# Revit family: Smoothy 1.6A
name_source: partatom
category: Lighting Fixtures
revit_build: Autodesk Revit 2017 (Build: 20160225_1515(x64)
units: mm (PartAtom-declared; Revit-internal decimal feet)

## family parameters
Cut with Voids When Loaded = Yes
Host = Face
Light Source = Yes
Part Type = Normal
Room Calculation Point = Yes
Round Connector Dimension = Use Diameter
Shared = No

## types (6) — shared parameters
Apparent Load = 0 VA
Apparent Load Phase 1 = 4 W
Body = L&L_Anodized aluminium
CRI = 90 (also available: CRI 80 - ref. URL Technical sheet)
Code = SY1600 I; SY1601 I
Color Filter = 16777215
Control system = -
Cutout dimensions = diam. 48 mm
Default Elevation = 1219 mm
Delivered lumen output = 141 lm (3000K, 22°, 2.5W, CRI 80);  125 lm (3000K, 22°, 2.5W, CRI 90);  188 lm (3000K, 22°, 3.5W, CRI 80);  165 lm (3000K, 22°, 3.5W, CRI 90)
Description = recessed for outdoor applications
Dimming Lamp Color Temperature Shift = <None>
Emit from Line Length = 610 mm
Energy efficiency class = A A+ A++
Features = -
Geometry = Smoothy1.6_mod
Height Void = 63 mm
Height mm = 64 mm  [stored 0.209974 ft]
IP = 67
LED Colour = 3000K (also available: 2700K and 4000K - ref. URL Technical sheet)
Length mm = 54 mm  [stored 0.177165 ft]
Lens = L&L_Tempered extra-clear glass
Lumen output at source = 168 lm (3000K, 2.5W, CRI 80); 147 lm (3000K, 2.5W, CRI 90); 224 lm (3000K, 3.5W, CRI 80); 196 lm (3000K, 3.5W, CRI 90);
Manufacturer = L&L Luce&Light
Material = body in anodized aluminium, trim in AISI 316L stainless steelscreen in tempered, transparent extra-clear glass (optics version), screen in sandblasted, tempered extra-clear glass (diffuse version)
Model = Smoothy 1.6
Mounting = recessed (ceiling, wall, ground)
No. and type of led = 1 power LED
Notes = -
Power = 3.5W (also available: 2.5W - ref. URL Technical sheet)
Power cables = includes 1.5 m neoprene cable H05RN-F 2x0.75/0.75 diam. 6.3 mm
Power supply = 24Vdc
Power supply unit = not included
Radius Void = 24 mm  [stored 0.0787402 ft]
Tilt Angle = 90.00°
Tiltable = -
Trim = L&L_Steel inox AISI 316L
URL = https://www.lucelight.it
URL Accessories and power supply units = https://www.lucelight.it
URL Catalogue = https://www.lucelight.it
URL DXF = https://www.lucelight.it
URL Description = https://www.lucelight.it
URL General code = https://www.lucelight.it
URL IES Photometric file = https://www.lucelight.it
URL Image = https://www.lucelight.it
URL Technical sheet = https://www.lucelight.it
Voltage = 24 V
Weight kg = 0.27
Width mm = 54 mm  [stored 0.177165 ft]
Wiring = parallel

## per-type parameters (varying)
| type | Optics | Photometric Web File |
| Smoothy 1.6_D (3000K 3.5W 24Vdc) | D | SMOOTHY 1.6 D [3000K 3.5W 24Vdc].IES |
| Smoothy 1.6_F 30° (3000K 3.5W 24Vdc) | 30° | SMOOTHY 1.6 F 30° [3000K 3.5W 24Vdc].IES |
| Smoothy 1.6_L 48° (3000K 3.5W 24Vdc) | 48° | SMOOTHY 1.6 L 48° [3000K 3.5W 24Vdc].IES |
| Smoothy 1.6_M 22° (3000K 3.5W 24Vdc) | 22° | SMOOTHY 1.6 M 22° [3000K 3.5W 24Vdc].IES |
| Smoothy 1.6_P 35° (3000K 3.5W 24Vdc) | 35° | SMOOTHY 1.6  P (35°) [3000K 3.5W 24Vdc].IES |
| Smoothy 1.6_S 13° (3000K 3.5W 24Vdc) | 13° | SMOOTHY 1.6  S 13° [3000K 3.5W 24Vdc].IES |

note: [stored X ft] marks values corroborated as IEEE doubles in the binary element streams (Revit-internal decimal feet)

## geometry (parser evidence)
native form markers: Blend x2, Sweep x6
no freeform markers — native parametric forms only
